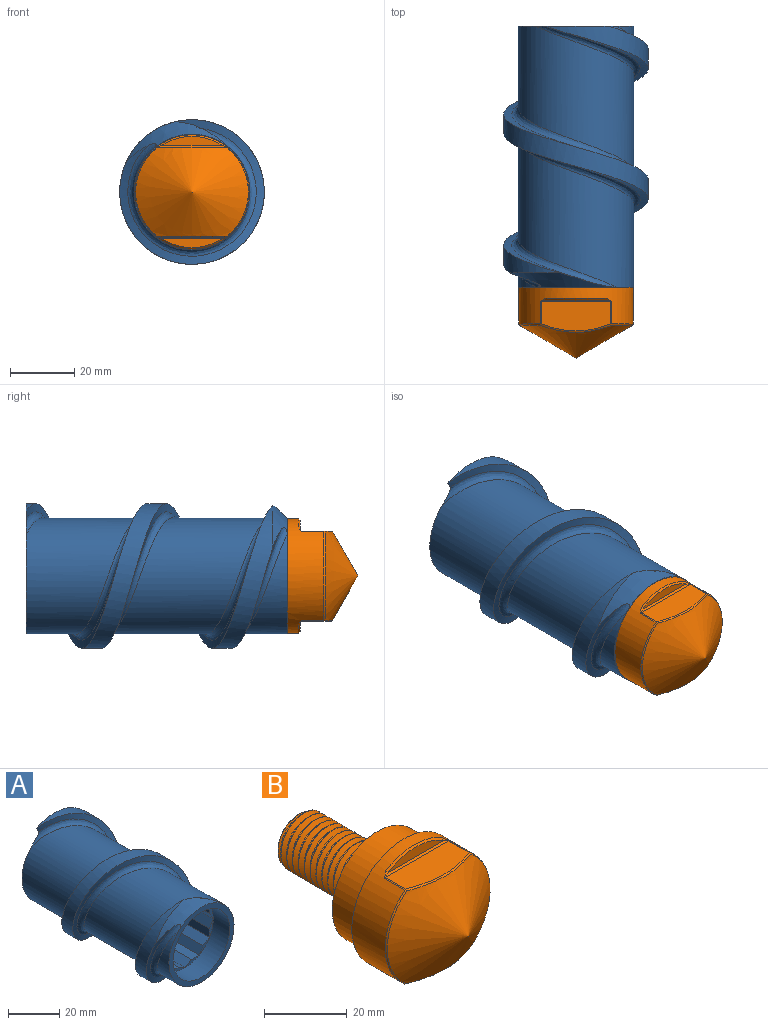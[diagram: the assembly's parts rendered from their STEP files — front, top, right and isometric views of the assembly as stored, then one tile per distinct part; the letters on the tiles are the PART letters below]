
ASSEMBLY  parts=2 mates=1
PART A: 35 faces, bbox 45x90x45 mm
  f0: cylinder r=22.5mm len=76.75mm, axis (0,1,0), area 1623.7mm2, adj f4,f5,f6,f34
  f1: plane 36x36mm, normal (0,-1,0), area 253.3mm2, adj f31,f33,f34
  f2: bspline ~90.02x40mm, area 753.6mm2, adj f4,f6,f31,f34
  f3: bspline ~86.64x40mm, area 753.2mm2, adj f5,f6,f31,f34
  f4: bspline ~84.64x45mm, area 669.9mm2, adj f0,f2,f6,f34
  f5: bspline ~81.25x45mm, area 669.4mm2, adj f0,f3,f6,f34
  f6: plane 40.5x36mm, normal (0,1,0), area 430.6mm2, adj f0,f2,f3,f4,f5,f7,f8,f9
  f7: plane 72.15x4.18mm, normal (0,0,-1), area 301.4mm2, adj f6,f8,f30,f32
  f8: plane 72.15x3.62mm, normal (-0.5,0,-0.87), area 301.4mm2, adj f6,f7,f9,f32
  f9: plane 72.15x3.62mm, normal (0.5,0,-0.87), area 301.4mm2, adj f6,f8,f10,f32
  f10: plane 72.15x4.18mm, normal (0,0,-1), area 301.4mm2, adj f6,f9,f11,f32
  f11: plane 72.15x3.62mm, normal (0.87,0,-0.5), area 301.4mm2, adj f6,f10,f12,f32
  f12: plane 72.15x3.62mm, normal (0.5,0,-0.87), area 301.4mm2, adj f6,f11,f13,f32
  f13: plane 72.15x4.18mm, normal (1,0,0), area 301.4mm2, adj f6,f12,f14,f32
  f14: plane 72.15x3.62mm, normal (0.87,0,-0.5), area 301.4mm2, adj f6,f13,f15,f32
  f15: plane 72.15x3.62mm, normal (0.87,0,0.5), area 301.4mm2, adj f6,f14,f16,f32
  f16: plane 72.15x4.18mm, normal (1,0,0), area 301.4mm2, adj f6,f15,f17,f32
  f17: plane 72.15x3.62mm, normal (0.5,0,0.87), area 301.4mm2, adj f6,f16,f18,f32
  f18: plane 72.15x3.62mm, normal (0.87,0,0.5), area 301.4mm2, adj f6,f17,f19,f32
  f19: plane 72.15x4.18mm, normal (0,0,1), area 301.4mm2, adj f6,f18,f20,f32
  f20: plane 72.15x3.62mm, normal (0.5,0,0.87), area 301.4mm2, adj f6,f19,f21,f32
  f21: plane 72.15x3.62mm, normal (-0.5,0,0.87), area 301.4mm2, adj f6,f20,f22,f32
  f22: plane 72.15x4.18mm, normal (0,0,1), area 301.4mm2, adj f6,f21,f23,f32
  f23: plane 72.15x3.62mm, normal (-0.87,0,0.5), area 301.4mm2, adj f6,f22,f24,f32
  f24: plane 72.15x3.62mm, normal (-0.5,0,0.87), area 301.4mm2, adj f6,f23,f25,f32
  f25: plane 72.15x4.18mm, normal (-1,0,0), area 301.4mm2, adj f6,f24,f26,f32
  f26: plane 72.15x3.62mm, normal (-0.87,0,0.5), area 301.4mm2, adj f6,f25,f27,f32
  f27: plane 72.15x3.62mm, normal (-0.87,0,-0.5), area 301.4mm2, adj f6,f26,f28,f32
  f28: plane 72.15x4.18mm, normal (-1,0,0), area 301.4mm2, adj f6,f27,f29,f32
  f29: plane 72.15x3.62mm, normal (-0.5,0,-0.87), area 301.4mm2, adj f6,f28,f30,f32
  f30: plane 72.15x3.62mm, normal (-0.87,0,-0.5), area 301.4mm2, adj f6,f7,f29,f32
  f31: cylinder r=18mm len=81.25mm, axis (0,-1,0), area 6934.4mm2, adj f1,f2,f3,f6
  f32: plane 31.2x31.2mm, normal (0,-1,0), area 87.9mm2, adj f7,f8,f9,f10,f11,f12,f13,f14
  f33: cylinder r=15.6mm len=31.2mm, axis (0,-1,0), area 892mm2, adj f1,f32
  f34: cone r=18mm half-angle=45deg, axis (0,1,0), area 126.6mm2, adj f0,f1,f2,f3,f4,f5
PART B: 39 faces, bbox 36.3x59.7x36.3 mm
  f0: plane 16.74x15.97mm, normal (0,-1,0), area 50.3mm2, adj f4,f5,f34,f36,f37
  f1: cylinder r=17.8mm len=35.6mm, axis (0,-1,0), area 900.7mm2, adj f8,f13,f15,f16,f17,f18,f22,f23
  f2: cone r=0mm half-angle=60deg, axis (0,1,0), area 1003.2mm2, adj f19,f22,f23,f24
  f3: plane 14.13x14.13mm, normal (0,1,0), area 151.9mm2, adj f33,f35,f37,f38
  f4: cylinder r=8mm len=22mm, axis (0,-1,0), area 12.4mm2, adj f0,f33,f34,f36,f38
  f5: cylinder r=6.5mm len=13mm, axis (0,-1,0), area 163.4mm2, adj f0,f6
  f6: plane 31x31mm, normal (0,1,0), area 622mm2, adj f5,f7
  f7: cylinder r=15.5mm len=31mm, axis (0,-1,0), area 876.5mm2, adj f6,f8
  f8: plane 35.6x35.6mm, normal (0,1,0), area 240.6mm2, adj f1,f7
  f9: plane 21.93x9.42mm, normal (0,0,-1), area 180.8mm2, adj f24,f27,f28,f29
  f10: plane 18.87x2.8mm, normal (0,-1,0), area 35.8mm2, adj f29,f32
  f11: plane 21.93x9.42mm, normal (0,0,1), area 180.8mm2, adj f14,f17,f18,f19
  f12: plane 18.87x2.8mm, normal (0,-1,0), area 35.8mm2, adj f13,f14
  f13: cone r=17.8mm half-angle=45deg, axis (0,1,0), area 14.3mm2, adj f1,f12,f15,f16
  f14: plane 21.64x0.5mm, normal (0,-0.71,0.71), area 14.3mm2, adj f11,f12,f15,f16
  f15: bspline ~1.73x1.08mm, area 0.7mm2, adj f1,f13,f14,f17
  f16: bspline ~1.7x1.03mm, area 0.7mm2, adj f1,f13,f14,f18
  f17: plane 6.93x0.31mm, normal (0.33,0,0.94), area 2.3mm2, adj f1,f11,f15,f20
  f18: plane 6.93x0.31mm, normal (-0.33,0,0.94), area 2.3mm2, adj f1,f11,f16,f21
  f19: bspline ~21.95x2.63mm, area 11.6mm2, adj f2,f11,f20,f21
  f20: plane 0.44x0.31mm, normal (0.29,-0.48,0.83), area 0.1mm2, adj f17,f19,f22
  f21: plane 0.43x0.31mm, normal (-0.29,-0.48,0.83), area 0.1mm2, adj f18,f19,f23
  f22: cone r=17.55mm half-angle=30deg, axis (0,1,0), area 15.8mm2, adj f1,f2,f20,f25
  f23: cone r=17.55mm half-angle=30deg, axis (0,1,0), area 15.8mm2, adj f1,f2,f21,f26
  f24: bspline ~21.95x2.63mm, area 11.6mm2, adj f2,f9,f25,f26
  f25: plane 0.43x0.31mm, normal (0.29,-0.48,-0.83), area 0.1mm2, adj f22,f24,f27
  f26: plane 0.43x0.31mm, normal (-0.29,-0.48,-0.83), area 0.1mm2, adj f23,f24,f28
  f27: plane 6.93x0.31mm, normal (0.33,0,-0.94), area 2.3mm2, adj f1,f9,f25,f30
  f28: plane 6.93x0.31mm, normal (-0.33,0,-0.94), area 2.3mm2, adj f1,f9,f26,f31
  f29: plane 21.64x0.5mm, normal (0,-0.71,-0.71), area 14.3mm2, adj f9,f10,f30,f31
  f30: bspline ~1.7x1.03mm, area 0.7mm2, adj f1,f27,f29,f32
  f31: bspline ~1.73x1.08mm, area 0.7mm2, adj f1,f28,f29,f32
  f32: cone r=17.8mm half-angle=45deg, axis (0,1,0), area 14.3mm2, adj f1,f10,f30,f31
  f33: cone r=8mm half-angle=45deg, axis (0,-1,0), area 27.2mm2, adj f3,f4,f35,f36,f38
  f34: plane 1.39x0.98mm, normal (0,0,1), area 0.8mm2, adj f0,f4,f37,f38
  f35: plane 1.39x1.02mm, normal (0,0,1), area 0.3mm2, adj f3,f33,f36,f37
  f36: bspline ~24.04x18.48mm, area 735.1mm2, adj f0,f4,f33,f35,f37
  f37: bspline ~23.83x15.64mm, area 290.1mm2, adj f0,f3,f34,f35,f36,f38
  f38: bspline ~23.71x18.48mm, area 724mm2, adj f3,f4,f33,f34,f37
PLACE A t=(-700,0,0)mm fixed
PLACE B t=(0,-81.25,0)mm
MATE fastened B.f1 <-> A.f0  axis (0,1,0) through (0,-81.25,0)mm
